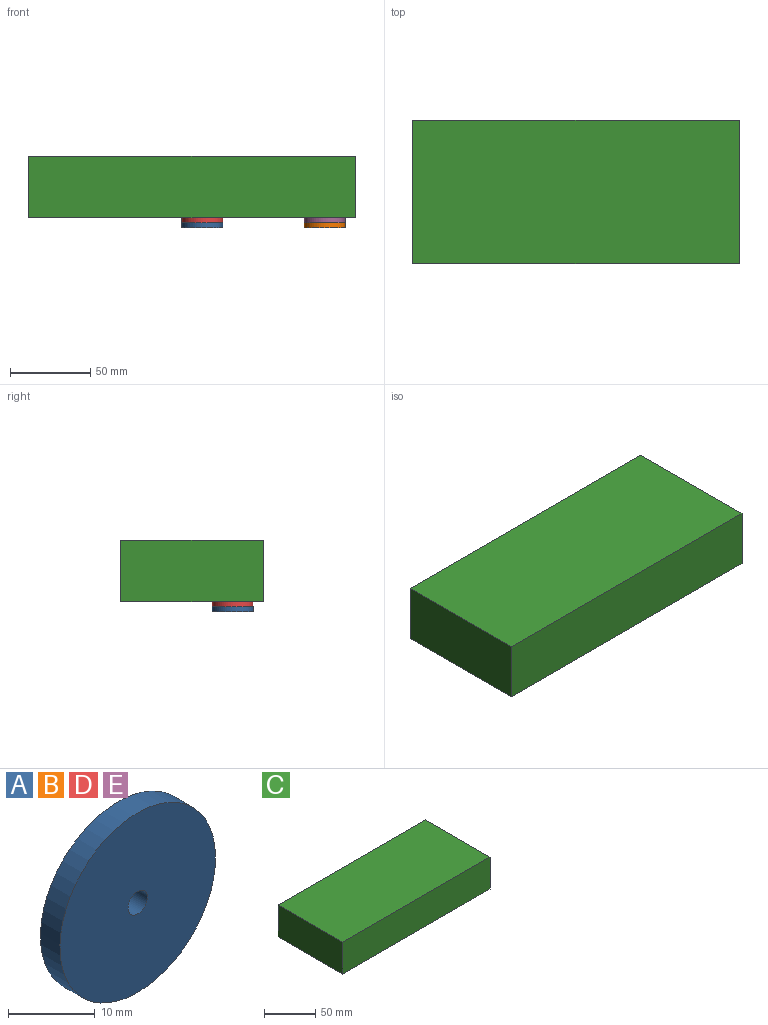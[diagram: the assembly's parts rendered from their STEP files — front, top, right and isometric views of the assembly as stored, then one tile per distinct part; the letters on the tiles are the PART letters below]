
ASSEMBLY  parts=5 mates=4
PART A: 4 faces, bbox 25.4x3.2x25.4 mm
  f0: cylinder r=1.59mm len=3.18mm, axis (0,1,0), area 31.7mm2, adj f2,f3
  f1: cylinder r=12.7mm len=25.4mm, axis (0,1,0), area 253.4mm2, adj f2,f3
  f2: plane 25.4x25.4mm, normal (0,-1,0), area 498.8mm2, adj f0,f1
  f3: plane 25.4x25.4mm, normal (0,1,0), area 498.8mm2, adj f0,f1
PART B: same geometry as A
PART C: 6 faces, bbox 203.2x88.9x38.1 mm
  f0: plane 203.2x38.1mm, normal (0,1,0), area 7741.9mm2, adj f1,f3,f4,f5
  f1: plane 203.2x88.9mm, normal (0,0,1), area 18064.5mm2, adj f0,f2,f4,f5
  f2: plane 203.2x38.1mm, normal (0,-1,0), area 7741.9mm2, adj f1,f3,f4,f5
  f3: plane 203.2x88.9mm, normal (0,0,-1), area 18064.5mm2, adj f0,f2,f4,f5
  f4: plane 88.9x38.1mm, normal (1,0,0), area 3387.1mm2, adj f0,f1,f2,f3
  f5: plane 88.9x38.1mm, normal (-1,0,0), area 3387.1mm2, adj f0,f1,f2,f3
PART D: same geometry as A
PART E: same geometry as A
PLACE A rot(axis=(-1,0,0),90deg) t=(6.35,-25.4,-44.45)mm
PLACE B rot(axis=(-0.14,0.7,-0.7),164.1deg) t=(82.55,-25.4,-44.45)mm
PLACE C t=(-101.6,0,-19.05)mm
PLACE D rot(axis=(1,0,0),90deg) t=(6.35,-25.4,-38.1)mm
PLACE E rot(axis=(1,0,0),90deg) t=(82.55,-25.4,-38.1)mm
MATE fastened E.f1 <-> C.f3  axis (0,0,1) through (82.55,-25.4,-38.1)mm
MATE revolute E.f1 <-> B.f1  axis (0,0,-1) through (82.55,-25.4,-41.28)mm
MATE fastened D.f1 <-> C.f3  axis (0,0,1) through (6.35,-25.4,-38.1)mm
MATE revolute A.f1 <-> D.f1  axis (0,0,1) through (6.35,-25.4,-41.28)mm
